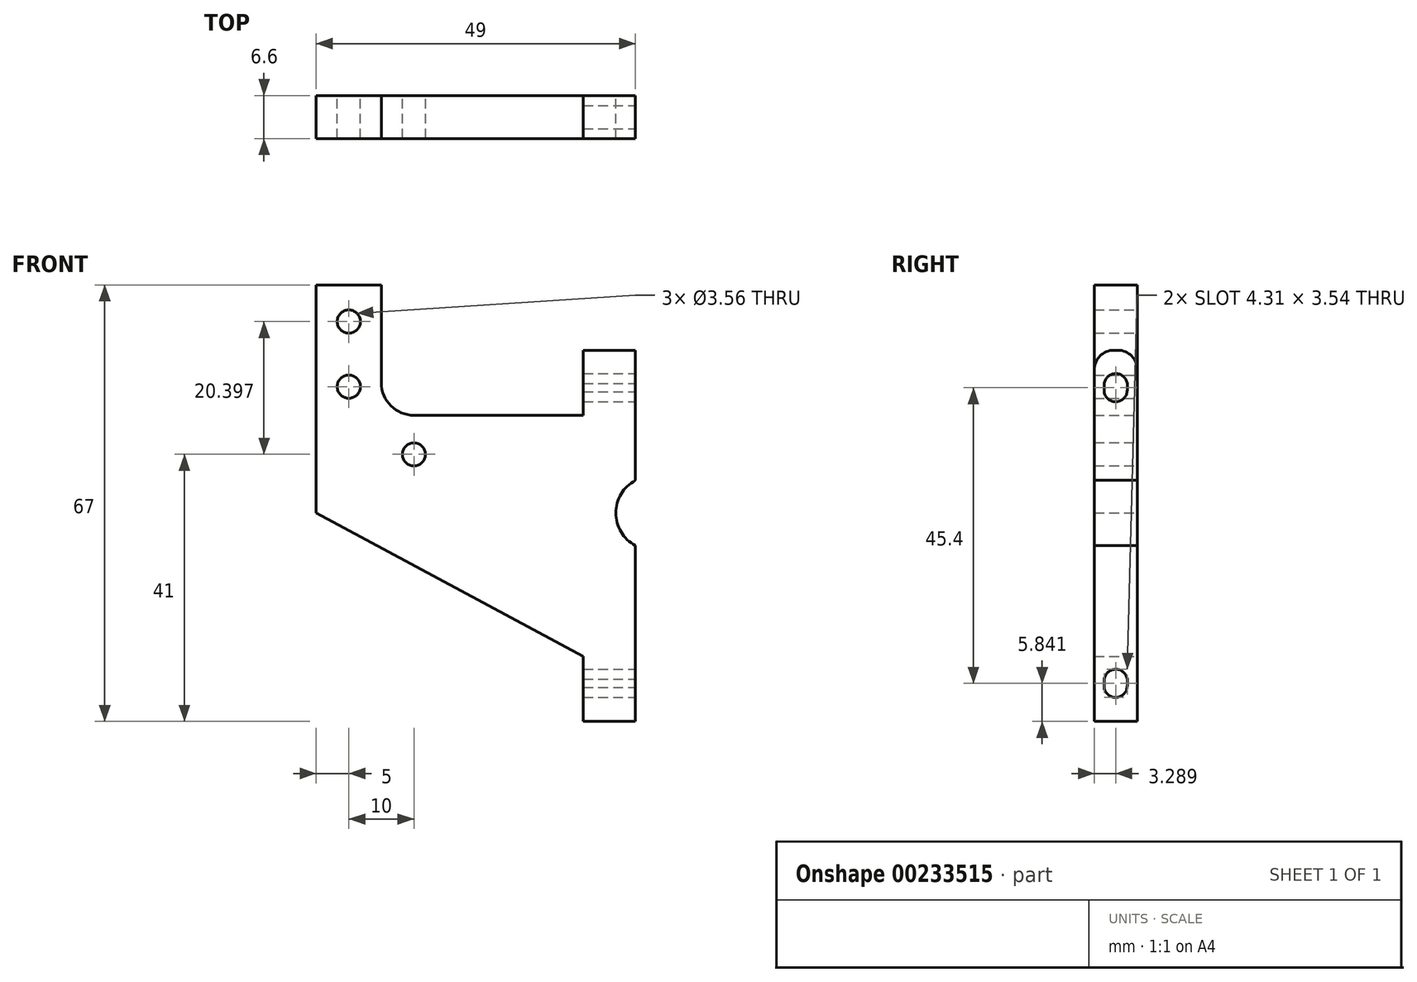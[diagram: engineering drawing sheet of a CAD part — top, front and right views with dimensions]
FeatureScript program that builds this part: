
annotation { "Feature Type Name" : "Feature", "Feature Type Description" : "" }
export const myFeature = defineFeature(function(context is Context, id is Id, definition is map)
    precondition{}
    {
        {
            var Q0;
            Q0=qCreatedBy(makeId("Front.planeOp"),FACE);
            var sketch = newSketch(context, id + "F0", { "sketchPlane" : qUnion([Q0])});
            skLineSegment(sketch, "E0.bottom", {"start": v(0, 0) * mm, "end": v(8, 0) * mm});
            skLineSegment(sketch, "E0.top", {"start": v(0, 57) * mm, "end": v(8, 57) * mm});
            skLineSegment(sketch, "E0.left", {"start": v(0, 0) * mm, "end": v(0, 10) * mm});
            skLineSegment(sketch, "E0.right", {"start": v(8, 0) * mm, "end": v(8, 27) * mm});
            skLineSegment(sketch, "E1", {"start": v(0, 10) * mm, "end": v(-41, 32) * mm});
            skLineSegment(sketch, "E2", {"start": v(-41, 32) * mm, "end": v(-41, 67) * mm});
            skLineSegment(sketch, "E3", {"start": v(-41, 67) * mm, "end": v(-31, 67) * mm});
            skLineSegment(sketch, "E4", {"start": v(-31, 67) * mm, "end": v(-31, 52) * mm});
            skLineSegment(sketch, "E5", {"start": v(-26, 47) * mm, "end": v(0, 47) * mm});
            skLineSegment(sketch, "E6.trimOffspring", {"start": v(0, 47) * mm, "end": v(0, 57) * mm});
            skArc(sketch, "E7", {"start": v(8, 37) * mm, "mid": v(5, 32) * mm, "end": v(8, 27) * mm});
            skLineSegment(sketch, "E8.trimOffspring", {"start": v(8, 37) * mm, "end": v(8, 57) * mm});
            skPoint(sketch, "E9.visualSharp", {"position": v(-31, 47) * mm});
            skArc(sketch, "E9.filletArc", {"start": v(-31, 52) * mm, "mid": v(-29.54, 48.46) * mm, "end": v(-26, 47) * mm});
            skCircle(sketch, "E10", {"center": v(-36, 61.4) * mm, "radius": 1.78 * mm});
            skCircle(sketch, "E11", {"center": v(-36, 51.4) * mm, "radius": 1.78 * mm});
            skCircle(sketch, "E12", {"center": v(-26, 41) * mm, "radius": 1.78 * mm});
            skSolve(sketch);
        }
        {
            var Q0;
            Q0 = qSketchRegion(id + "F0", true);
            extrude(context, id + "F1", {"entities" : qUnion([Q0]), "depth" : 6.6 * mm});
        }
        {
            var Q0;
            Q0=makeQuery(id+"F1.opExtrude","SWEPT_FACE",FACE,{"disambiguationData":[OSD([sQuery(id+"F0.wireOp",EDGE,"E8.trimOffspring")])]});
            var sketch = newSketch(context, id + "F2", { "sketchPlane" : qUnion([Q0])});
            skLineSegment(sketch, "E13.0", {"start": v(-1.54, 51.9) * mm, "end": v(-1.54, 50.86) * mm});
            skArc(sketch, "E14.0", {"start": v(-5.08, 51.62) * mm, "mid": v(-3.44, 53.4) * mm, "end": v(-1.54, 51.9) * mm});
            skLineSegment(sketch, "E15.0", {"start": v(-5.08, 50.59) * mm, "end": v(-5.08, 51.62) * mm});
            skArc(sketch, "E16.0", {"start": v(-1.54, 50.86) * mm, "mid": v(-3.18, 49.09) * mm, "end": v(-5.08, 50.59) * mm});
            skArc(sketch, "E17.0.1.0", {"start": v(-1.54, 5.46) * mm, "mid": v(-3.18, 3.69) * mm, "end": v(-5.08, 5.19) * mm});
            skArc(sketch, "E17.0.1.1", {"start": v(-5.08, 6.22) * mm, "mid": v(-3.44, 8) * mm, "end": v(-1.54, 6.5) * mm});
            skLineSegment(sketch, "E17.0.1.2", {"start": v(-5.08, 5.19) * mm, "end": v(-5.08, 6.22) * mm});
            skLineSegment(sketch, "E17.0.1.3", {"start": v(-1.54, 6.5) * mm, "end": v(-1.54, 5.46) * mm});
            skLineSegment(sketch, "E17.direction1", {"start": v(-5.08, 51.62) * mm, "end": v(19.22, 51.62) * mm, "construction": true});
            skLineSegment(sketch, "E17.direction2", {"start": v(-5.08, 51.62) * mm, "end": v(-5.08, 6.22) * mm, "construction": true});
            skSolve(sketch);
        }
        {
            var Q0;
            Q0 = qSketchRegion(id + "F2", true);
            extrude(context, id + "F3", {"entities" : qUnion([Q0]), "operationType" : NewBodyOperationType.REMOVE, "endBound" : BoundingType.UP_TO_NEXT, "oppositeDirection" : true, "depth" : 25 * mm});
        }
        {
            var Q0;
            Q0=makeQuery(id+"F1.opExtrude","CAP_EDGE",EDGE,{"disambiguationData":[OSD([sQuery(id+"F0.wireOp",EDGE,"E0.top")])],"isStart":true});
            var Q1;
            Q1=makeQuery(id+"F1.opExtrude","CAP_EDGE",EDGE,{"disambiguationData":[OSD([sQuery(id+"F0.wireOp",EDGE,"E0.top")])],"isStart":false});
            fillet(context, id + "F4", {"entities" : qUnion([Q0, Q1]), "radius" : 3 * mm, "tangentPropagation" : true, "allowEdgeOverflow" : false});
        }
    });
